# Revit family: 206_Classic-lapivienti
name_source: partatom
category: Duct Accessories
units: mm (PartAtom-declared; Revit-internal decimal feet)

## family parameters
Always vertical = Yes
Cut with Voids When Loaded = No
Part Type = Breaks Into
Round Connector Dimension = Use Diameter
Shared = No
Work Plane-Based = No

## types (1)
- VILPE CLASSIC PASS-THROUGH
    CAT0 = Yes
    D = 110 mm
    Description = Pass-through seal
    H2 = 56 mm  [stored 0.183727 ft]
    H2D = 351 mm
    L = 10 mm  [stored 0.0328084 ft]
    L2D = 10 mm  [stored 0.0328084 ft]
    MC Product Code = VILPE CLASSIC PASS-THROUGH
    Manufacturer = Vilpe
    QmdConnectorList = 201;D;202;D
    THW = 43 mm
    URL = http://www.vilpe.com
    W12 = 48 mm  [stored 0.15748 ft]
    W2 = 133 mm  [stored 0.436352 ft]
    W2D = 266 mm  [stored 0.872703 ft]
    WL = 85 mm  [stored 0.278871 ft]
    magiPartTypeId = 206
    magiProductFamilyId = Classic-lapivienti
    magiProductId = Classic-lapivienti

note: [stored X ft] marks values corroborated as IEEE doubles in the binary element streams (Revit-internal decimal feet)

## geometry (parser evidence)
native form markers: Sweep x2
no freeform markers — native parametric forms only
